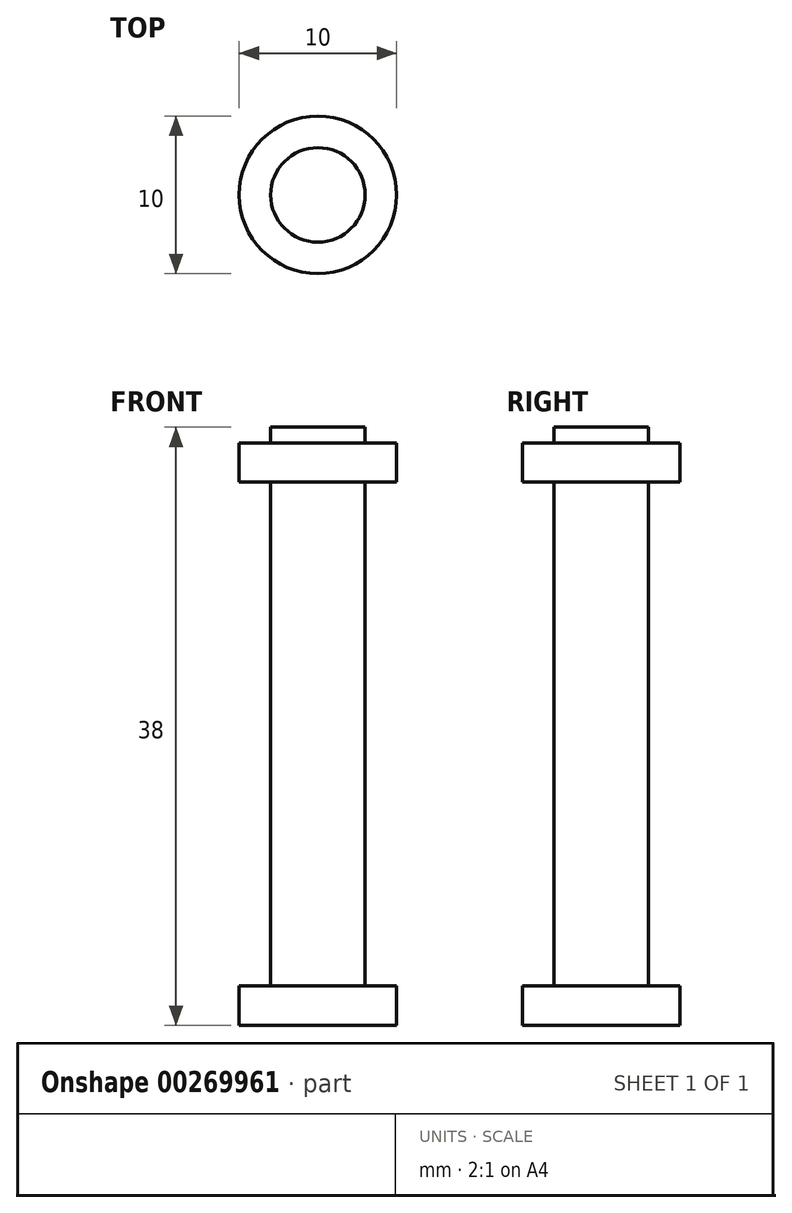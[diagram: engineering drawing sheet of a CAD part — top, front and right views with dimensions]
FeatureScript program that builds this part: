
annotation { "Feature Type Name" : "Feature", "Feature Type Description" : "" }
export const myFeature = defineFeature(function(context is Context, id is Id, definition is map)
    precondition{}
    {
        {
            var Q0;
            Q0=qCreatedBy(makeId("Front.planeOp"),FACE);
            var sketch = newSketch(context, id + "F0", { "sketchPlane" : qUnion([Q0])});
            skLineSegment(sketch, "E0", {"start": v(-3, 16) * mm, "end": v(-3, -16) * mm});
            skLineSegment(sketch, "E1", {"start": v(-3, 16) * mm, "end": v(0, 16) * mm});
            skLineSegment(sketch, "E2", {"start": v(-3, -16) * mm, "end": v(0, -16) * mm});
            skLineSegment(sketch, "E3", {"start": v(-3, 16) * mm, "end": v(-5, 16) * mm});
            skLineSegment(sketch, "E4", {"start": v(-5, 16) * mm, "end": v(-5, 18.5) * mm});
            skLineSegment(sketch, "E5", {"start": v(-5, 18.5) * mm, "end": v(0, 18.5) * mm});
            skLineSegment(sketch, "E6.MirrorCS", {"start": v(-5, -18.5) * mm, "end": v(0, -18.5) * mm});
            skLineSegment(sketch, "E7.MirrorCS", {"start": v(-5, -16) * mm, "end": v(-5, -18.5) * mm});
            skLineSegment(sketch, "E8.MirrorCS", {"start": v(-3, -16) * mm, "end": v(-5, -16) * mm});
            skLineSegment(sketch, "E9", {"start": v(-3, 18.5) * mm, "end": v(-3, 19.5) * mm});
            skLineSegment(sketch, "E10", {"start": v(-3, 19.5) * mm, "end": v(0, 19.5) * mm});
            skLineSegment(sketch, "E11", {"start": v(0, 19.5) * mm, "end": v(0, -18.5) * mm});
            skSolve(sketch);
        }
        {
            var Q0;
            Q0=qSketchRegion(id+"F0",true);
            var Q1;
            Q1=sQuery(id+"F0.wireOp",EDGE,"E11");
            revolve(context, id + "F1", {"entities" : qUnion([Q0]), "axis" : qUnion([Q1]), "revolveType" : RevolveType.FULL});
        }
    });
